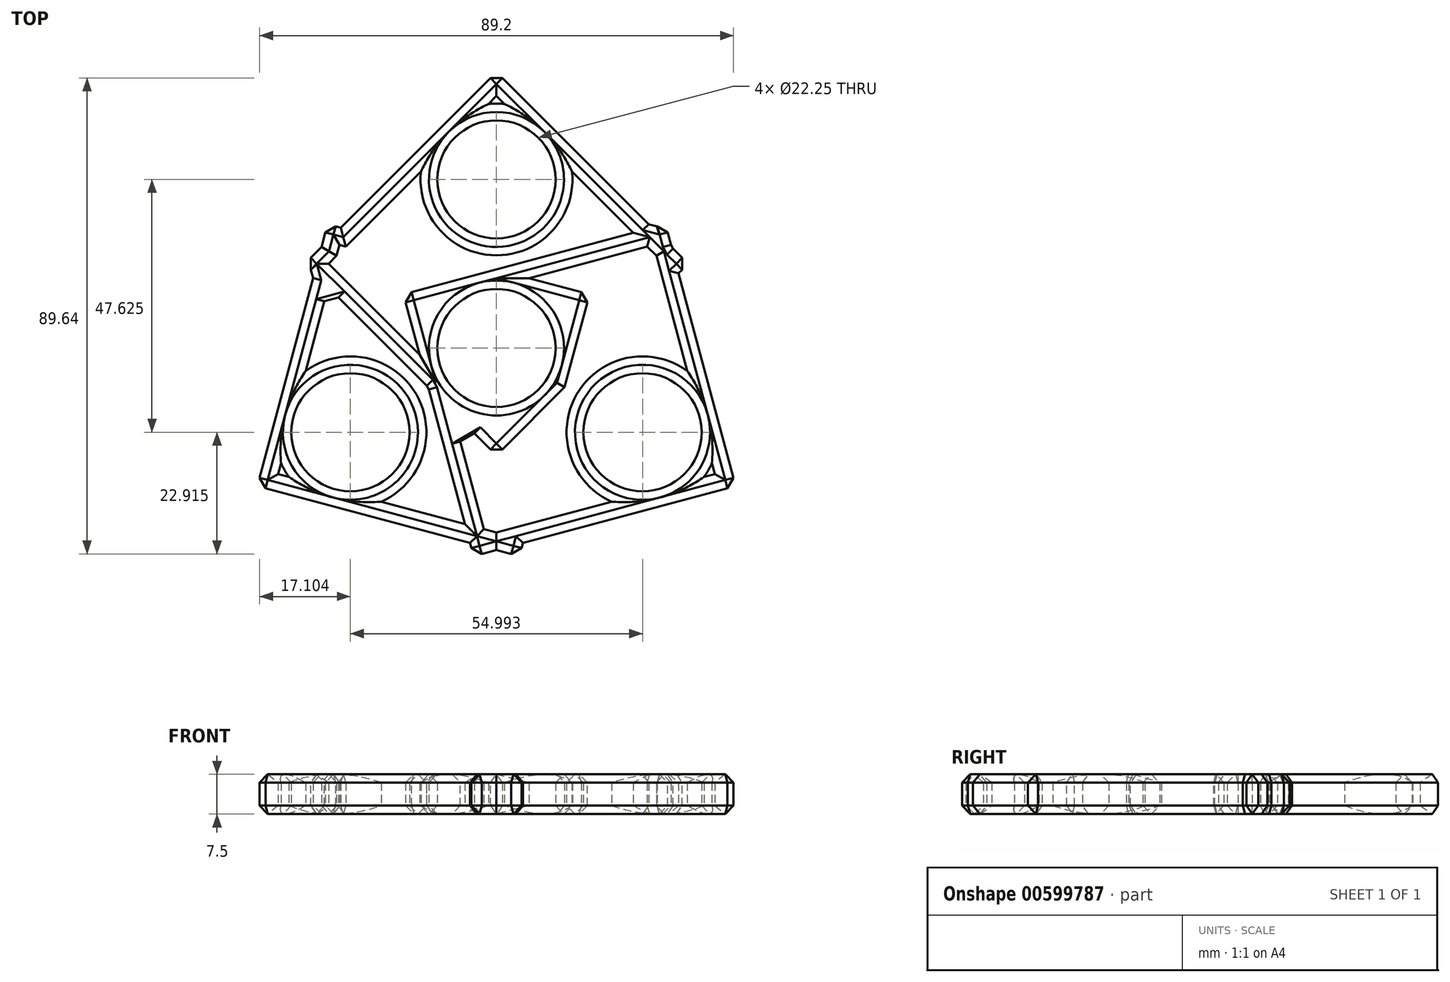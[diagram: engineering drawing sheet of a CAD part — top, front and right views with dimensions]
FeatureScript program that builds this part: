
annotation { "Feature Type Name" : "Feature", "Feature Type Description" : "" }
export const myFeature = defineFeature(function(context is Context, id is Id, definition is map)
    precondition{}
    {
        {
            var Q0;
            Q0=qCreatedBy(makeId("Top.planeOp"),FACE);
            var sketch = newSketch(context, id + "F0", { "sketchPlane" : qUnion([Q0])});
            skCircle(sketch, "E0", {"center": v(0, 0) * mm, "radius": 11.12 * mm});
            skCircle(sketch, "E1", {"center": v(0, 31.75) * mm, "radius": 11.12 * mm});
            skCircle(sketch, "E2", {"center": v(0, 31.75) * mm, "radius": 14.3 * mm});
            skCircle(sketch, "E3", {"center": v(0, 0) * mm, "radius": 14.3 * mm});
            skLineSegment(sketch, "E4", {"start": v(0, 51.97) * mm, "end": v(-36.1, 15.87) * mm});
            skLineSegment(sketch, "E5", {"start": v(0, 51.97) * mm, "end": v(36.1, 15.88) * mm});
            skLineSegment(sketch, "E6", {"start": v(0, -20.22) * mm, "end": v(36.1, 15.88) * mm});
            skLineSegment(sketch, "E7", {"start": v(36.1, 15.88) * mm, "end": v(0, -20.22) * mm});
            skLineSegment(sketch, "E8", {"start": v(0, -20.22) * mm, "end": v(-36.1, 15.88) * mm});
            skLineSegment(sketch, "E9", {"start": v(0, 47.48) * mm, "end": v(-31.6, 15.88) * mm});
            skLineSegment(sketch, "E10", {"start": v(-31.6, 15.87) * mm, "end": v(0, 47.48) * mm});
            skLineSegment(sketch, "E11", {"start": v(0, 47.48) * mm, "end": v(31.6, 15.88) * mm});
            skLineSegment(sketch, "E12", {"start": v(0, -15.73) * mm, "end": v(31.6, 15.87) * mm});
            skLineSegment(sketch, "E13", {"start": v(0, -15.73) * mm, "end": v(-31.6, 15.87) * mm});
            skCircle(sketch, "E14.1.0", {"center": v(-27.5, -15.87) * mm, "radius": 11.12 * mm});
            skCircle(sketch, "E14.1.1", {"center": v(-27.5, -15.87) * mm, "radius": 14.3 * mm});
            skLineSegment(sketch, "E14.1.2", {"start": v(-41.12, -23.74) * mm, "end": v(-29.55, 19.44) * mm});
            skLineSegment(sketch, "E14.1.3", {"start": v(-45.01, -25.99) * mm, "end": v(-31.8, 23.32) * mm});
            skLineSegment(sketch, "E14.1.4", {"start": v(13.63, 7.87) * mm, "end": v(-29.55, 19.44) * mm});
            skLineSegment(sketch, "E14.1.5", {"start": v(17.51, 10.11) * mm, "end": v(-31.8, 23.32) * mm});
            skLineSegment(sketch, "E14.1.6", {"start": v(17.51, 10.11) * mm, "end": v(4.3, -39.2) * mm});
            skLineSegment(sketch, "E14.1.7", {"start": v(13.63, 7.87) * mm, "end": v(2.06, -35.31) * mm});
            skLineSegment(sketch, "E14.1.8", {"start": v(-41.12, -23.74) * mm, "end": v(2.06, -35.31) * mm});
            skLineSegment(sketch, "E14.1.9", {"start": v(-45.01, -25.99) * mm, "end": v(4.3, -39.2) * mm});
            skCircle(sketch, "E14.2.0", {"center": v(27.5, -15.88) * mm, "radius": 11.12 * mm});
            skCircle(sketch, "E14.2.1", {"center": v(27.5, -15.88) * mm, "radius": 14.3 * mm});
            skLineSegment(sketch, "E14.2.2", {"start": v(41.12, -23.74) * mm, "end": v(-2.06, -35.31) * mm});
            skLineSegment(sketch, "E14.2.3", {"start": v(45.01, -25.99) * mm, "end": v(-4.3, -39.2) * mm});
            skLineSegment(sketch, "E14.2.4", {"start": v(-13.63, 7.87) * mm, "end": v(-2.06, -35.31) * mm});
            skLineSegment(sketch, "E14.2.5", {"start": v(-17.51, 10.11) * mm, "end": v(-4.3, -39.2) * mm});
            skLineSegment(sketch, "E14.2.6", {"start": v(-17.51, 10.11) * mm, "end": v(31.8, 23.32) * mm});
            skLineSegment(sketch, "E14.2.7", {"start": v(-13.63, 7.87) * mm, "end": v(29.55, 19.44) * mm});
            skLineSegment(sketch, "E14.2.8", {"start": v(41.12, -23.74) * mm, "end": v(29.55, 19.44) * mm});
            skLineSegment(sketch, "E14.2.9", {"start": v(45.01, -25.99) * mm, "end": v(31.8, 23.32) * mm});
            skSolve(sketch);
        }
        {
            var Q0;
            Q0 = qSketchRegion(id + "F0", true);
            var Q1;
            {var subQ0=sQuery(id+"F0.wireOp",EDGE,"E10");var subQ1=sQuery(id+"F0.wireOp",EDGE,"E1");var subQ2=makeQuery(id+"F0.imprint","INTERSECT",VERTEX,{"derivedFrom":[subQ1,subQ0]});Q1=makeQuery(id+"F0.imprint","IMPRINT",FACE,{"disambiguationData":[TD([[makeQuery(id+"F0.imprint","IMPRINT",EDGE,{"disambiguationData":[TD([[subQ2,-1.0]])],"derivedFrom":subQ1}),-1.0]])]});}
            var Q2;
            {var subQ0=sQuery(id+"F0.wireOp",EDGE,"E10");var subQ1=sQuery(id+"F0.wireOp",EDGE,"E1");var subQ2=makeQuery(id+"F0.imprint","INTERSECT",VERTEX,{"derivedFrom":[subQ1,subQ0]});Q2=makeQuery(id+"F0.imprint","IMPRINT",FACE,{"disambiguationData":[TD([[makeQuery(id+"F0.imprint","IMPRINT",EDGE,{"disambiguationData":[TD([[subQ2,1.0]])],"derivedFrom":subQ1}),-1.0]])]});}
            var Q3;
            {var subQ0=sQuery(id+"F0.wireOp",EDGE,"E14.2.2");var subQ1=sQuery(id+"F0.wireOp",EDGE,"E14.2.0");var subQ2=makeQuery(id+"F0.imprint","INTERSECT",VERTEX,{"derivedFrom":[subQ1,subQ0]});Q3=makeQuery(id+"F0.imprint","IMPRINT",FACE,{"disambiguationData":[TD([[makeQuery(id+"F0.imprint","IMPRINT",EDGE,{"disambiguationData":[TD([[subQ2,1.0]])],"derivedFrom":subQ1}),-1.0]])]});}
            var Q4;
            {var subQ0=sQuery(id+"F0.wireOp",EDGE,"E14.2.2");var subQ1=sQuery(id+"F0.wireOp",EDGE,"E14.2.0");var subQ2=makeQuery(id+"F0.imprint","INTERSECT",VERTEX,{"derivedFrom":[subQ1,subQ0]});Q4=makeQuery(id+"F0.imprint","IMPRINT",FACE,{"disambiguationData":[TD([[makeQuery(id+"F0.imprint","IMPRINT",EDGE,{"disambiguationData":[TD([[subQ2,-1.0]])],"derivedFrom":subQ1}),-1.0]])]});}
            var Q5;
            {var subQ0=sQuery(id+"F0.wireOp",EDGE,"E14.1.2");var subQ1=sQuery(id+"F0.wireOp",EDGE,"E14.1.0");var subQ2=makeQuery(id+"F0.imprint","INTERSECT",VERTEX,{"derivedFrom":[subQ1,subQ0]});Q5=makeQuery(id+"F0.imprint","IMPRINT",FACE,{"disambiguationData":[TD([[makeQuery(id+"F0.imprint","IMPRINT",EDGE,{"disambiguationData":[TD([[subQ2,1.0]])],"derivedFrom":subQ1}),-1.0]])]});}
            var Q6;
            {var subQ0=sQuery(id+"F0.wireOp",EDGE,"E14.1.2");var subQ1=sQuery(id+"F0.wireOp",EDGE,"E14.1.0");var subQ2=makeQuery(id+"F0.imprint","INTERSECT",VERTEX,{"derivedFrom":[subQ1,subQ0]});Q6=makeQuery(id+"F0.imprint","IMPRINT",FACE,{"disambiguationData":[TD([[makeQuery(id+"F0.imprint","IMPRINT",EDGE,{"disambiguationData":[TD([[subQ2,-1.0]])],"derivedFrom":subQ1}),-1.0]])]});}
            var Q7;
            {var subQ2=sQuery(id+"F0.wireOp",EDGE,"E14.1.4");var subQ5=sQuery(id+"F0.wireOp",EDGE,"E10");var subQ8=makeQuery(id+"F0.imprint","INTERSECT",VERTEX,{"derivedFrom":[subQ5,subQ2]});Q7=makeQuery(id+"F0.imprint","IMPRINT",FACE,{"disambiguationData":[TD([[makeQuery(id+"F0.imprint","IMPRINT",EDGE,{"disambiguationData":[TD([[subQ8,-1.0]])],"derivedFrom":subQ5}),-1.0]])]});}
            var Q8;
            {var subQ1=sQuery(id+"F0.wireOp",EDGE,"E7");var subQ7=makeQuery(id+"F0.imprint","INTERSECT",VERTEX,{"derivedFrom":[sQuery(id+"F0.wireOp",EDGE,"E3"),subQ1]});Q8=makeQuery(id+"F0.imprint","IMPRINT",FACE,{"disambiguationData":[TD([[makeQuery(id+"F0.imprint","IMPRINT",EDGE,{"disambiguationData":[TD([[subQ7,1.0]])],"derivedFrom":subQ1}),1.0]])]});}
            var Q9;
            {var subQ2=sQuery(id+"F0.wireOp",EDGE,"E7");var subQ6=sQuery(id+"F0.wireOp",EDGE,"E14.2.8");var subQ8=makeQuery(id+"F0.imprint","INTERSECT",VERTEX,{"derivedFrom":[subQ2,subQ6]});Q9=makeQuery(id+"F0.imprint","IMPRINT",FACE,{"disambiguationData":[TD([[makeQuery(id+"F0.imprint","IMPRINT",EDGE,{"disambiguationData":[TD([[subQ8,-1.0]])],"derivedFrom":subQ2}),-1.0]])]});}
            var Q10;
            {var subQ0=sQuery(id+"F0.wireOp",EDGE,"E14.2.6");var subQ1=sQuery(id+"F0.wireOp",EDGE,"E11");var subQ2=makeQuery(id+"F0.imprint","INTERSECT",VERTEX,{"derivedFrom":[subQ1,subQ0]});Q10=makeQuery(id+"F0.imprint","IMPRINT",FACE,{"disambiguationData":[TD([[makeQuery(id+"F0.imprint","IMPRINT",EDGE,{"disambiguationData":[TD([[subQ2,-1.0]])],"derivedFrom":subQ1}),-1.0]])]});}
            var Q11;
            {var subQ0=sQuery(id+"F0.wireOp",EDGE,"E3");var subQ4=sQuery(id+"F0.wireOp",EDGE,"E14.2.7");var subQ7=makeQuery(id+"F0.imprint","INTERSECT",VERTEX,{"disambiguationData":[OD(0.0)],"derivedFrom":[subQ0,subQ4]});Q11=makeQuery(id+"F0.imprint","IMPRINT",FACE,{"disambiguationData":[TD([[makeQuery(id+"F0.imprint","IMPRINT",EDGE,{"disambiguationData":[TD([[subQ7,-1.0]])],"derivedFrom":subQ0}),1.0]])]});}
            var Q12;
            {var subQ0=sQuery(id+"F0.wireOp",EDGE,"E13");var subQ1=sQuery(id+"F0.wireOp",EDGE,"E3");var subQ2=makeQuery(id+"F0.imprint","INTERSECT",VERTEX,{"disambiguationData":[OD(0.0)],"derivedFrom":[subQ1,subQ0]});Q12=makeQuery(id+"F0.imprint","IMPRINT",FACE,{"disambiguationData":[TD([[makeQuery(id+"F0.imprint","IMPRINT",EDGE,{"disambiguationData":[TD([[subQ2,-1.0]])],"derivedFrom":subQ1}),1.0]])]});}
            var Q13;
            {var subQ0=sQuery(id+"F0.wireOp",EDGE,"E3");var subQ4=sQuery(id+"F0.wireOp",EDGE,"E14.1.7");var subQ7=makeQuery(id+"F0.imprint","INTERSECT",VERTEX,{"disambiguationData":[OD(1.0)],"derivedFrom":[subQ0,subQ4]});Q13=makeQuery(id+"F0.imprint","IMPRINT",FACE,{"disambiguationData":[TD([[makeQuery(id+"F0.imprint","IMPRINT",EDGE,{"disambiguationData":[TD([[subQ7,-1.0]])],"derivedFrom":subQ0}),1.0]])]});}
            var Q14;
            {var subQ0=sQuery(id+"F0.wireOp",EDGE,"E14.1.5");var subQ1=sQuery(id+"F0.wireOp",EDGE,"E3");var subQ2=makeQuery(id+"F0.imprint","INTERSECT",VERTEX,{"derivedFrom":[subQ1,subQ0]});Q14=makeQuery(id+"F0.imprint","IMPRINT",FACE,{"disambiguationData":[TD([[makeQuery(id+"F0.imprint","IMPRINT",EDGE,{"disambiguationData":[TD([[subQ2,-1.0]])],"derivedFrom":subQ1}),-1.0]])]});}
            var Q15;
            {var subQ0=sQuery(id+"F0.wireOp",EDGE,"E14.2.5");var subQ1=sQuery(id+"F0.wireOp",EDGE,"E3");var subQ2=makeQuery(id+"F0.imprint","INTERSECT",VERTEX,{"derivedFrom":[subQ1,subQ0]});Q15=makeQuery(id+"F0.imprint","IMPRINT",FACE,{"disambiguationData":[TD([[makeQuery(id+"F0.imprint","IMPRINT",EDGE,{"disambiguationData":[TD([[subQ2,-1.0]])],"derivedFrom":subQ1}),-1.0]])]});}
            var Q16;
            {var subQ0=sQuery(id+"F0.wireOp",EDGE,"E7");var subQ1=sQuery(id+"F0.wireOp",EDGE,"E3");var subQ2=makeQuery(id+"F0.imprint","INTERSECT",VERTEX,{"derivedFrom":[subQ1,subQ0]});Q16=makeQuery(id+"F0.imprint","IMPRINT",FACE,{"disambiguationData":[TD([[makeQuery(id+"F0.imprint","IMPRINT",EDGE,{"disambiguationData":[TD([[subQ2,-1.0]])],"derivedFrom":subQ1}),-1.0]])]});}
            var Q17;
            {var subQ0=sQuery(id+"F0.wireOp",EDGE,"E14.2.7");var subQ1=sQuery(id+"F0.wireOp",EDGE,"E0");var subQ2=makeQuery(id+"F0.imprint","INTERSECT",VERTEX,{"derivedFrom":[subQ1,subQ0]});Q17=makeQuery(id+"F0.imprint","IMPRINT",FACE,{"disambiguationData":[TD([[makeQuery(id+"F0.imprint","IMPRINT",EDGE,{"disambiguationData":[TD([[subQ2,-1.0]])],"derivedFrom":subQ1}),-1.0]])]});}
            var Q18;
            {var subQ0=sQuery(id+"F0.wireOp",EDGE,"E14.2.4");var subQ1=sQuery(id+"F0.wireOp",EDGE,"E3");var subQ2=makeQuery(id+"F0.imprint","INTERSECT",VERTEX,{"disambiguationData":[OD(0.0)],"derivedFrom":[subQ1,subQ0]});Q18=makeQuery(id+"F0.imprint","IMPRINT",FACE,{"disambiguationData":[TD([[makeQuery(id+"F0.imprint","IMPRINT",EDGE,{"disambiguationData":[TD([[subQ2,-1.0]])],"derivedFrom":subQ1}),1.0]])]});}
            var Q19;
            {var subQ0=sQuery(id+"F0.wireOp",EDGE,"E14.1.4");var subQ1=sQuery(id+"F0.wireOp",EDGE,"E3");var subQ2=makeQuery(id+"F0.imprint","INTERSECT",VERTEX,{"disambiguationData":[OD(1.0)],"derivedFrom":[subQ1,subQ0]});Q19=makeQuery(id+"F0.imprint","IMPRINT",FACE,{"disambiguationData":[TD([[makeQuery(id+"F0.imprint","IMPRINT",EDGE,{"disambiguationData":[TD([[subQ2,-1.0]])],"derivedFrom":subQ1}),1.0]])]});}
            var Q20;
            {var subQ0=sQuery(id+"F0.wireOp",EDGE,"E14.1.4");var subQ1=sQuery(id+"F0.wireOp",EDGE,"E3");var subQ2=makeQuery(id+"F0.imprint","INTERSECT",VERTEX,{"disambiguationData":[OD(0.0)],"derivedFrom":[subQ1,subQ0]});Q20=makeQuery(id+"F0.imprint","IMPRINT",FACE,{"disambiguationData":[TD([[makeQuery(id+"F0.imprint","IMPRINT",EDGE,{"disambiguationData":[TD([[subQ2,-1.0]])],"derivedFrom":subQ1}),1.0]])]});}
            var Q21;
            {var subQ0=sQuery(id+"F0.wireOp",EDGE,"E14.1.7");var subQ1=sQuery(id+"F0.wireOp",EDGE,"E3");var subQ2=makeQuery(id+"F0.imprint","INTERSECT",VERTEX,{"disambiguationData":[OD(0.0)],"derivedFrom":[subQ1,subQ0]});Q21=makeQuery(id+"F0.imprint","IMPRINT",FACE,{"disambiguationData":[TD([[makeQuery(id+"F0.imprint","IMPRINT",EDGE,{"disambiguationData":[TD([[subQ2,1.0]])],"derivedFrom":subQ1}),1.0]])]});}
            var Q22;
            {var subQ0=sQuery(id+"F0.wireOp",EDGE,"E14.1.4");var subQ1=sQuery(id+"F0.wireOp",EDGE,"E0");var subQ2=makeQuery(id+"F0.imprint","INTERSECT",VERTEX,{"derivedFrom":[subQ1,subQ0]});Q22=makeQuery(id+"F0.imprint","IMPRINT",FACE,{"disambiguationData":[TD([[makeQuery(id+"F0.imprint","IMPRINT",EDGE,{"disambiguationData":[TD([[subQ2,1.0]])],"derivedFrom":subQ1}),-1.0]])]});}
            var Q23;
            {var subQ0=sQuery(id+"F0.wireOp",EDGE,"E12");var subQ1=sQuery(id+"F0.wireOp",EDGE,"E3");var subQ2=makeQuery(id+"F0.imprint","INTERSECT",VERTEX,{"disambiguationData":[OD(0.0)],"derivedFrom":[subQ1,subQ0]});Q23=makeQuery(id+"F0.imprint","IMPRINT",FACE,{"disambiguationData":[TD([[makeQuery(id+"F0.imprint","IMPRINT",EDGE,{"disambiguationData":[TD([[subQ2,-1.0]])],"derivedFrom":subQ1}),1.0]])]});}
            var Q24;
            {var subQ0=sQuery(id+"F0.wireOp",EDGE,"E13");var subQ1=sQuery(id+"F0.wireOp",EDGE,"E0");var subQ2=makeQuery(id+"F0.imprint","INTERSECT",VERTEX,{"derivedFrom":[subQ1,subQ0]});Q24=makeQuery(id+"F0.imprint","IMPRINT",FACE,{"disambiguationData":[TD([[makeQuery(id+"F0.imprint","IMPRINT",EDGE,{"disambiguationData":[TD([[subQ2,-1.0]])],"derivedFrom":subQ1}),-1.0]])]});}
            var Q25;
            {var subQ1=sQuery(id+"F0.wireOp",EDGE,"E8");var subQ7=makeQuery(id+"F0.imprint","INTERSECT",VERTEX,{"derivedFrom":[sQuery(id+"F0.wireOp",EDGE,"E3"),subQ1]});Q25=makeQuery(id+"F0.imprint","IMPRINT",FACE,{"disambiguationData":[TD([[makeQuery(id+"F0.imprint","IMPRINT",EDGE,{"disambiguationData":[TD([[subQ7,1.0]])],"derivedFrom":subQ1}),1.0]])]});}
            var Q26;
            {var subQ0=sQuery(id+"F0.wireOp",EDGE,"E14.2.4");var subQ1=sQuery(id+"F0.wireOp",EDGE,"E3");var subQ2=makeQuery(id+"F0.imprint","INTERSECT",VERTEX,{"disambiguationData":[OD(1.0)],"derivedFrom":[subQ1,subQ0]});Q26=makeQuery(id+"F0.imprint","IMPRINT",FACE,{"disambiguationData":[TD([[makeQuery(id+"F0.imprint","IMPRINT",EDGE,{"disambiguationData":[TD([[subQ2,-1.0]])],"derivedFrom":subQ1}),1.0]])]});}
            var Q27;
            {var subQ0=sQuery(id+"F0.wireOp",EDGE,"E14.2.4");var subQ1=sQuery(id+"F0.wireOp",EDGE,"E0");var subQ2=makeQuery(id+"F0.imprint","INTERSECT",VERTEX,{"derivedFrom":[subQ1,subQ0]});Q27=makeQuery(id+"F0.imprint","IMPRINT",FACE,{"disambiguationData":[TD([[makeQuery(id+"F0.imprint","IMPRINT",EDGE,{"disambiguationData":[TD([[subQ2,-1.0]])],"derivedFrom":subQ1}),-1.0]])]});}
            var Q28;
            {var subQ0=sQuery(id+"F0.wireOp",EDGE,"E14.2.7");var subQ1=sQuery(id+"F0.wireOp",EDGE,"E0");var subQ2=makeQuery(id+"F0.imprint","INTERSECT",VERTEX,{"derivedFrom":[subQ1,subQ0]});Q28=makeQuery(id+"F0.imprint","IMPRINT",FACE,{"disambiguationData":[TD([[makeQuery(id+"F0.imprint","IMPRINT",EDGE,{"disambiguationData":[TD([[subQ2,1.0]])],"derivedFrom":subQ1}),-1.0]])]});}
            var Q29;
            {var subQ0=sQuery(id+"F0.wireOp",EDGE,"E12");var subQ1=sQuery(id+"F0.wireOp",EDGE,"E0");var subQ2=makeQuery(id+"F0.imprint","INTERSECT",VERTEX,{"derivedFrom":[subQ1,subQ0]});Q29=makeQuery(id+"F0.imprint","IMPRINT",FACE,{"disambiguationData":[TD([[makeQuery(id+"F0.imprint","IMPRINT",EDGE,{"disambiguationData":[TD([[subQ2,-1.0]])],"derivedFrom":subQ1}),-1.0]])]});}
            var Q30;
            {var subQ0=sQuery(id+"F0.wireOp",EDGE,"E14.1.4");var subQ1=sQuery(id+"F0.wireOp",EDGE,"E3");var subQ2=makeQuery(id+"F0.imprint","INTERSECT",VERTEX,{"disambiguationData":[OD(1.0)],"derivedFrom":[subQ1,subQ0]});Q30=makeQuery(id+"F0.imprint","IMPRINT",FACE,{"disambiguationData":[TD([[makeQuery(id+"F0.imprint","IMPRINT",EDGE,{"disambiguationData":[TD([[subQ2,-1.0]])],"derivedFrom":subQ1}),-1.0]])]});}
            var Q31;
            {var subQ1=sQuery(id+"F0.wireOp",EDGE,"E14.1.4");var subQ3=sQuery(id+"F0.wireOp",EDGE,"E3");var subQ4=makeQuery(id+"F0.imprint","INTERSECT",VERTEX,{"disambiguationData":[OD(0.0)],"derivedFrom":[subQ3,subQ1]});Q31=makeQuery(id+"F0.imprint","IMPRINT",FACE,{"disambiguationData":[TD([[makeQuery(id+"F0.imprint","IMPRINT",EDGE,{"disambiguationData":[TD([[subQ4,-1.0]])],"derivedFrom":subQ3}),-1.0]])]});}
            var Q32;
            {var subQ3=sQuery(id+"F0.wireOp",EDGE,"E14.2.4");var subQ6=sQuery(id+"F0.wireOp",EDGE,"E3");var subQ10=makeQuery(id+"F0.imprint","INTERSECT",VERTEX,{"disambiguationData":[OD(1.0)],"derivedFrom":[subQ6,subQ3]});Q32=makeQuery(id+"F0.imprint","IMPRINT",FACE,{"disambiguationData":[TD([[makeQuery(id+"F0.imprint","IMPRINT",EDGE,{"disambiguationData":[TD([[subQ10,-1.0]])],"derivedFrom":subQ6}),-1.0]])]});}
            var Q33;
            {var subQ1=sQuery(id+"F0.wireOp",EDGE,"E8");var subQ5=sQuery(id+"F0.wireOp",EDGE,"E14.2.5");var subQ8=makeQuery(id+"F0.imprint","INTERSECT",VERTEX,{"derivedFrom":[subQ1,subQ5]});Q33=makeQuery(id+"F0.imprint","IMPRINT",FACE,{"disambiguationData":[TD([[makeQuery(id+"F0.imprint","IMPRINT",EDGE,{"disambiguationData":[TD([[subQ8,-1.0]])],"derivedFrom":subQ1}),-1.0]])]});}
            var Q34;
            {var subQ0=sQuery(id+"F0.wireOp",EDGE,"E13");var subQ1=sQuery(id+"F0.wireOp",EDGE,"E3");var subQ2=makeQuery(id+"F0.imprint","INTERSECT",VERTEX,{"disambiguationData":[OD(0.0)],"derivedFrom":[subQ1,subQ0]});Q34=makeQuery(id+"F0.imprint","IMPRINT",FACE,{"disambiguationData":[TD([[makeQuery(id+"F0.imprint","IMPRINT",EDGE,{"disambiguationData":[TD([[subQ2,-1.0]])],"derivedFrom":subQ1}),-1.0]])]});}
            var Q35;
            {var subQ0=sQuery(id+"F0.wireOp",EDGE,"E8");var subQ1=sQuery(id+"F0.wireOp",EDGE,"E3");var subQ2=makeQuery(id+"F0.imprint","INTERSECT",VERTEX,{"derivedFrom":[subQ1,subQ0]});Q35=makeQuery(id+"F0.imprint","IMPRINT",FACE,{"disambiguationData":[TD([[makeQuery(id+"F0.imprint","IMPRINT",EDGE,{"disambiguationData":[TD([[subQ2,-1.0]])],"derivedFrom":subQ1}),-1.0]])]});}
            var Q36;
            {var subQ0=sQuery(id+"F0.wireOp",EDGE,"E14.1.7");var subQ1=sQuery(id+"F0.wireOp",EDGE,"E3");var subQ2=makeQuery(id+"F0.imprint","INTERSECT",VERTEX,{"disambiguationData":[OD(1.0)],"derivedFrom":[subQ1,subQ0]});Q36=makeQuery(id+"F0.imprint","IMPRINT",FACE,{"disambiguationData":[TD([[makeQuery(id+"F0.imprint","IMPRINT",EDGE,{"disambiguationData":[TD([[subQ2,-1.0]])],"derivedFrom":subQ1}),-1.0]])]});}
            var Q37;
            {var subQ0=sQuery(id+"F0.wireOp",EDGE,"E14.1.6");var subQ1=sQuery(id+"F0.wireOp",EDGE,"E3");var subQ2=makeQuery(id+"F0.imprint","INTERSECT",VERTEX,{"derivedFrom":[subQ1,subQ0]});Q37=makeQuery(id+"F0.imprint","IMPRINT",FACE,{"disambiguationData":[TD([[makeQuery(id+"F0.imprint","IMPRINT",EDGE,{"disambiguationData":[TD([[subQ2,-1.0]])],"derivedFrom":subQ1}),-1.0]])]});}
            var Q38;
            {var subQ0=sQuery(id+"F0.wireOp",EDGE,"E14.2.7");var subQ1=sQuery(id+"F0.wireOp",EDGE,"E3");var subQ2=makeQuery(id+"F0.imprint","INTERSECT",VERTEX,{"disambiguationData":[OD(0.0)],"derivedFrom":[subQ1,subQ0]});Q38=makeQuery(id+"F0.imprint","IMPRINT",FACE,{"disambiguationData":[TD([[makeQuery(id+"F0.imprint","IMPRINT",EDGE,{"disambiguationData":[TD([[subQ2,-1.0]])],"derivedFrom":subQ1}),-1.0]])]});}
            var Q39;
            {var subQ0=sQuery(id+"F0.wireOp",EDGE,"E14.2.6");var subQ1=sQuery(id+"F0.wireOp",EDGE,"E3");var subQ2=makeQuery(id+"F0.imprint","INTERSECT",VERTEX,{"derivedFrom":[subQ1,subQ0]});Q39=makeQuery(id+"F0.imprint","IMPRINT",FACE,{"disambiguationData":[TD([[makeQuery(id+"F0.imprint","IMPRINT",EDGE,{"disambiguationData":[TD([[subQ2,-1.0]])],"derivedFrom":subQ1}),-1.0]])]});}
            var Q40;
            {var subQ0=sQuery(id+"F0.wireOp",EDGE,"E14.1.2");var subQ1=sQuery(id+"F0.wireOp",EDGE,"E10");var subQ2=makeQuery(id+"F0.imprint","INTERSECT",VERTEX,{"derivedFrom":[subQ1,subQ0]});Q40=makeQuery(id+"F0.imprint","IMPRINT",FACE,{"disambiguationData":[TD([[makeQuery(id+"F0.imprint","IMPRINT",EDGE,{"disambiguationData":[TD([[subQ2,-1.0]])],"derivedFrom":subQ1}),1.0]])]});}
            var Q41;
            {var subQ0=sQuery(id+"F0.wireOp",EDGE,"E13");var subQ1=sQuery(id+"F0.wireOp",EDGE,"E10");var subQ2=makeQuery(id+"F0.imprint","INTERSECT",VERTEX,{"derivedFrom":[subQ1,subQ0]});Q41=makeQuery(id+"F0.imprint","IMPRINT",FACE,{"disambiguationData":[TD([[makeQuery(id+"F0.imprint","IMPRINT",EDGE,{"disambiguationData":[TD([[subQ2,-1.0]])],"derivedFrom":subQ1}),-1.0]])]});}
            var Q42;
            {var subQ0=sQuery(id+"F0.wireOp",EDGE,"E14.2.7");var subQ1=sQuery(id+"F0.wireOp",EDGE,"E11");var subQ2=makeQuery(id+"F0.imprint","INTERSECT",VERTEX,{"derivedFrom":[subQ1,subQ0]});Q42=makeQuery(id+"F0.imprint","IMPRINT",FACE,{"disambiguationData":[TD([[makeQuery(id+"F0.imprint","IMPRINT",EDGE,{"disambiguationData":[TD([[subQ2,-1.0]])],"derivedFrom":subQ1}),1.0]])]});}
            var Q43;
            {var subQ0=sQuery(id+"F0.wireOp",EDGE,"E12");var subQ1=sQuery(id+"F0.wireOp",EDGE,"E11");var subQ2=makeQuery(id+"F0.imprint","INTERSECT",VERTEX,{"derivedFrom":[subQ1,subQ0]});Q43=makeQuery(id+"F0.imprint","IMPRINT",FACE,{"disambiguationData":[TD([[makeQuery(id+"F0.imprint","IMPRINT",EDGE,{"disambiguationData":[TD([[subQ2,1.0]])],"derivedFrom":subQ1}),-1.0]])]});}
            var Q44;
            {var subQ0=sQuery(id+"F0.wireOp",EDGE,"E14.2.4");var subQ1=sQuery(id+"F0.wireOp",EDGE,"E14.1.8");var subQ2=makeQuery(id+"F0.imprint","INTERSECT",VERTEX,{"derivedFrom":[subQ1,subQ0]});Q44=makeQuery(id+"F0.imprint","IMPRINT",FACE,{"disambiguationData":[TD([[makeQuery(id+"F0.imprint","IMPRINT",EDGE,{"disambiguationData":[TD([[subQ2,-1.0]])],"derivedFrom":subQ1}),-1.0]])]});}
            var Q45;
            {var subQ0=sQuery(id+"F0.wireOp",EDGE,"E14.1.8");var subQ1=sQuery(id+"F0.wireOp",EDGE,"E14.1.7");var subQ2=makeQuery(id+"F0.imprint","INTERSECT",VERTEX,{"derivedFrom":[subQ1,subQ0]});Q45=makeQuery(id+"F0.imprint","IMPRINT",FACE,{"disambiguationData":[TD([[makeQuery(id+"F0.imprint","IMPRINT",EDGE,{"disambiguationData":[TD([[subQ2,1.0]])],"derivedFrom":subQ1}),-1.0]])]});}
            extrude(context, id + "F1", {"entities" : qUnion([Q0, Q1, Q2, Q3, Q4, Q5, Q6, Q7, Q8, Q9, Q10, Q11, Q12, Q13, Q14, Q15, Q16, Q17, Q18, Q19, Q20, Q21, Q22, Q23, Q24, Q25, Q26, Q27, Q28, Q29, Q30, Q31, Q32, Q33, Q34, Q35, Q36, Q37, Q38, Q39, Q40, Q41, Q42, Q43, Q44, Q45]), "depth" : 7.5 * mm, "offsetDistance" : 25.4 * mm});
        }
        {
            var Q0;
            Q0=makeQuery(id+"F1.opExtrude","CAP_FACE",FACE,{"disambiguationData":[OSD([sQuery(id+"F0.wireOp",EDGE,"E0"),sQuery(id+"F0.wireOp",EDGE,"E1"),sQuery(id+"F0.wireOp",EDGE,"E2"),sQuery(id+"F0.wireOp",EDGE,"E3"),sQuery(id+"F0.wireOp",EDGE,"E4"),sQuery(id+"F0.wireOp",EDGE,"E5"),sQuery(id+"F0.wireOp",EDGE,"E7"),sQuery(id+"F0.wireOp",EDGE,"E8"),sQuery(id+"F0.wireOp",EDGE,"E10"),sQuery(id+"F0.wireOp",EDGE,"E11"),sQuery(id+"F0.wireOp",EDGE,"E12"),sQuery(id+"F0.wireOp",EDGE,"E13"),sQuery(id+"F0.wireOp",EDGE,"E14.1.0"),sQuery(id+"F0.wireOp",EDGE,"E14.1.1"),sQuery(id+"F0.wireOp",EDGE,"E14.1.2"),sQuery(id+"F0.wireOp",EDGE,"E14.1.3"),sQuery(id+"F0.wireOp",EDGE,"E14.1.4"),sQuery(id+"F0.wireOp",EDGE,"E14.1.5"),sQuery(id+"F0.wireOp",EDGE,"E14.1.6"),sQuery(id+"F0.wireOp",EDGE,"E14.1.7"),sQuery(id+"F0.wireOp",EDGE,"E14.1.8"),sQuery(id+"F0.wireOp",EDGE,"E14.1.9"),sQuery(id+"F0.wireOp",EDGE,"E14.2.0"),sQuery(id+"F0.wireOp",EDGE,"E14.2.1"),sQuery(id+"F0.wireOp",EDGE,"E14.2.2"),sQuery(id+"F0.wireOp",EDGE,"E14.2.3"),sQuery(id+"F0.wireOp",EDGE,"E14.2.4"),sQuery(id+"F0.wireOp",EDGE,"E14.2.5"),sQuery(id+"F0.wireOp",EDGE,"E14.2.6"),sQuery(id+"F0.wireOp",EDGE,"E14.2.7"),sQuery(id+"F0.wireOp",EDGE,"E14.2.8"),sQuery(id+"F0.wireOp",EDGE,"E14.2.9")])],"isStart":false});
            var Q1;
            Q1=makeQuery(id+"F1.opExtrude","CAP_FACE",FACE,{"disambiguationData":[OSD([sQuery(id+"F0.wireOp",EDGE,"E0"),sQuery(id+"F0.wireOp",EDGE,"E1"),sQuery(id+"F0.wireOp",EDGE,"E2"),sQuery(id+"F0.wireOp",EDGE,"E3"),sQuery(id+"F0.wireOp",EDGE,"E4"),sQuery(id+"F0.wireOp",EDGE,"E5"),sQuery(id+"F0.wireOp",EDGE,"E7"),sQuery(id+"F0.wireOp",EDGE,"E8"),sQuery(id+"F0.wireOp",EDGE,"E10"),sQuery(id+"F0.wireOp",EDGE,"E11"),sQuery(id+"F0.wireOp",EDGE,"E12"),sQuery(id+"F0.wireOp",EDGE,"E13"),sQuery(id+"F0.wireOp",EDGE,"E14.1.0"),sQuery(id+"F0.wireOp",EDGE,"E14.1.1"),sQuery(id+"F0.wireOp",EDGE,"E14.1.2"),sQuery(id+"F0.wireOp",EDGE,"E14.1.3"),sQuery(id+"F0.wireOp",EDGE,"E14.1.4"),sQuery(id+"F0.wireOp",EDGE,"E14.1.5"),sQuery(id+"F0.wireOp",EDGE,"E14.1.6"),sQuery(id+"F0.wireOp",EDGE,"E14.1.7"),sQuery(id+"F0.wireOp",EDGE,"E14.1.8"),sQuery(id+"F0.wireOp",EDGE,"E14.1.9"),sQuery(id+"F0.wireOp",EDGE,"E14.2.0"),sQuery(id+"F0.wireOp",EDGE,"E14.2.1"),sQuery(id+"F0.wireOp",EDGE,"E14.2.2"),sQuery(id+"F0.wireOp",EDGE,"E14.2.3"),sQuery(id+"F0.wireOp",EDGE,"E14.2.4"),sQuery(id+"F0.wireOp",EDGE,"E14.2.5"),sQuery(id+"F0.wireOp",EDGE,"E14.2.6"),sQuery(id+"F0.wireOp",EDGE,"E14.2.7"),sQuery(id+"F0.wireOp",EDGE,"E14.2.8"),sQuery(id+"F0.wireOp",EDGE,"E14.2.9")])],"isStart":true});
            var Q2;
            Q2=makeQuery(id+"F1.opExtrude","SWEPT_EDGE",EDGE,{"disambiguationData":[OSD([sQuery(id+"F0.wireOp",EDGE,"E14.2.3"),sQuery(id+"F0.wireOp",EDGE,"E14.2.9")])]});
            var Q3;
            Q3=makeQuery(id+"F1.opExtrude","SWEPT_EDGE",EDGE,{"disambiguationData":[OSD([sQuery(id+"F0.wireOp",EDGE,"E5"),sQuery(id+"F0.wireOp",EDGE,"E7")])]});
            var Q4;
            Q4=makeQuery(id+"F1.opExtrude","SWEPT_EDGE",EDGE,{"disambiguationData":[OSD([sQuery(id+"F0.wireOp",EDGE,"E14.2.6"),sQuery(id+"F0.wireOp",EDGE,"E14.2.9")])]});
            var Q5;
            Q5=makeQuery(id+"F1.opExtrude","SWEPT_EDGE",EDGE,{"disambiguationData":[OSD([sQuery(id+"F0.wireOp",EDGE,"E14.1.6"),sQuery(id+"F0.wireOp",EDGE,"E14.1.9")])]});
            var Q6;
            Q6=makeQuery(id+"F1.opExtrude","SWEPT_EDGE",EDGE,{"disambiguationData":[OSD([sQuery(id+"F0.wireOp",EDGE,"E14.2.3"),sQuery(id+"F0.wireOp",EDGE,"E14.2.5")])]});
            var Q7;
            Q7=makeQuery(id+"F1.opExtrude","SWEPT_EDGE",EDGE,{"disambiguationData":[OSD([sQuery(id+"F0.wireOp",EDGE,"E14.1.3"),sQuery(id+"F0.wireOp",EDGE,"E14.1.9")])]});
            var Q8;
            Q8=makeQuery(id+"F1.opExtrude","SWEPT_EDGE",EDGE,{"disambiguationData":[OSD([sQuery(id+"F0.wireOp",EDGE,"E4"),sQuery(id+"F0.wireOp",EDGE,"E8")])]});
            var Q9;
            Q9=makeQuery(id+"F1.opExtrude","SWEPT_EDGE",EDGE,{"disambiguationData":[OSD([sQuery(id+"F0.wireOp",EDGE,"E14.1.3"),sQuery(id+"F0.wireOp",EDGE,"E14.1.5")])]});
            var Q10;
            Q10=makeQuery(id+"F1.opExtrude","SWEPT_EDGE",EDGE,{"disambiguationData":[OSD([sQuery(id+"F0.wireOp",EDGE,"E4"),sQuery(id+"F0.wireOp",EDGE,"E5")])]});
            var Q11;
            Q11=makeQuery(id+"F1.opExtrude","SWEPT_EDGE",EDGE,{"disambiguationData":[OSD([sQuery(id+"F0.wireOp",EDGE,"E14.2.5"),sQuery(id+"F0.wireOp",EDGE,"E14.2.6")])]});
            var Q12;
            Q12=makeQuery(id+"F1.opExtrude","SWEPT_EDGE",EDGE,{"disambiguationData":[OSD([sQuery(id+"F0.wireOp",EDGE,"E7"),sQuery(id+"F0.wireOp",EDGE,"E8")])]});
            var Q13;
            Q13=makeQuery(id+"F1.opExtrude","SWEPT_EDGE",EDGE,{"disambiguationData":[OSD([sQuery(id+"F0.wireOp",EDGE,"E14.1.5"),sQuery(id+"F0.wireOp",EDGE,"E14.1.6")])]});
            chamfer(context, id + "F2", {"entities" : qUnion([Q0, Q1, Q2, Q3, Q4, Q5, Q6, Q7, Q8, Q9, Q10, Q11, Q12, Q13]), "width" : 1.59 * mm, "tangentPropagation" : true});
        }
    });
